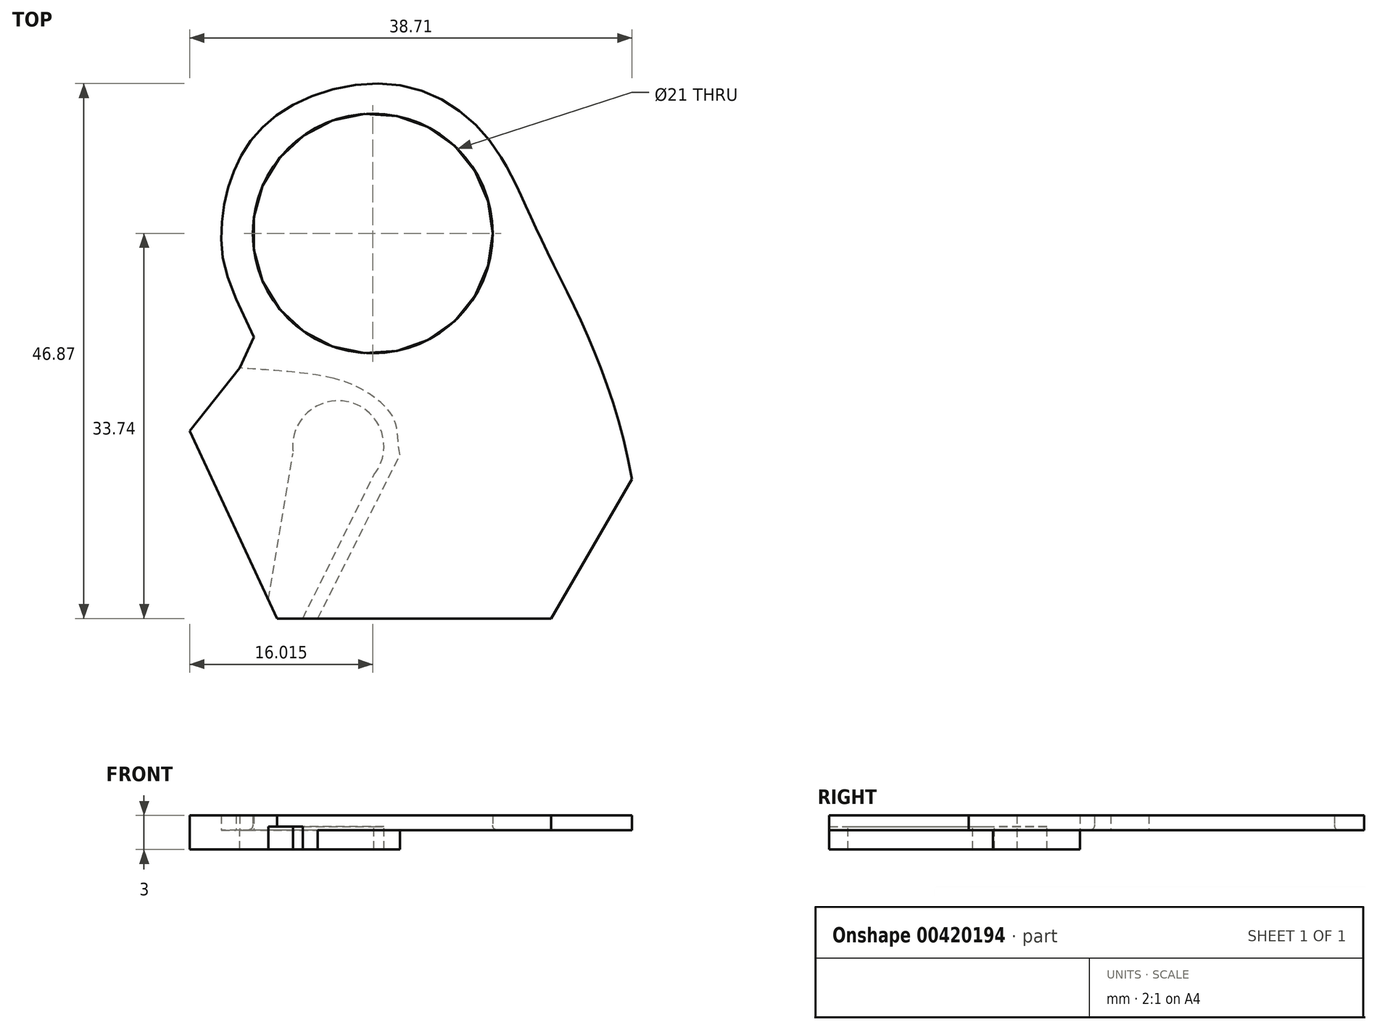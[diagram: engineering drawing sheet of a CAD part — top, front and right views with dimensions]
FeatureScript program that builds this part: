
annotation { "Feature Type Name" : "Feature", "Feature Type Description" : "" }
export const myFeature = defineFeature(function(context is Context, id is Id, definition is map)
    precondition{}
    {
        {
            var Q0;
            Q0=qCreatedBy(makeId("Top.planeOp"),FACE);
            var sketch = newSketch(context, id + "F0", { "sketchPlane" : qUnion([Q0])});
            skLineSegment(sketch, "E0", {"start": v(-18.43, -12.2) * mm, "end": v(5.57, -12.2) * mm});
            skLineSegment(sketch, "E1", {"start": v(5.57, -12.2) * mm, "end": v(12.63, 0) * mm});
            skLineSegment(sketch, "E2", {"start": v(-18.43, -12.2) * mm, "end": v(-26.08, 4.22) * mm});
            skLineSegment(sketch, "E3", {"start": v(-26.08, 4.22) * mm, "end": v(-21.72, 9.75) * mm});
            skLineSegment(sketch, "E4", {"start": v(-21.72, 9.75) * mm, "end": v(-20.49, 12.46) * mm});
            skLineSegment(sketch, "E5", {"start": v(-20.49, 12.46) * mm, "end": v(-22.02, 15.79) * mm});
            skPoint(sketch, "E6", {"position": v(-14.21, 11.55) * mm});
            skPoint(sketch, "E7", {"position": v(0, 25.65) * mm});
            skPoint(sketch, "E8", {"position": v(-2.76, 13.99) * mm});
            skCircle(sketch, "E9", {"center": v(-13.08, 2.87) * mm, "radius": 4 * mm});
            skLineSegment(sketch, "E10", {"start": v(-19.2, -10.55) * mm, "end": v(-17.04, 2.25) * mm});
            skCircle(sketch, "E11", {"center": v(-10.06, 21.53) * mm, "radius": 10.5 * mm});
            skFitSpline(sketch, "E12", {"points": [v(12.63, 0) * mm, v(4.58, 21.25) * mm, v(0, 29.89) * mm, v(-7.31, 34.44) * mm, v(-16.64, 33) * mm, v(-21.43, 28.61) * mm, v(-23.23, 23.05) * mm, v(-22.02, 15.79) * mm], "startDerivative": vector(-21.08, 123.93) * mm, "endDerivative": vector(32.5, -68.62) * mm});
            skLineSegment(sketch, "E13", {"start": v(-16.19, -12.2) * mm, "end": v(-9.96, 0.37) * mm});
            skLineSegment(sketch, "E14", {"start": v(-14.87, -12.2) * mm, "end": v(-7.68, 2.12) * mm});
            skFitSpline(sketch, "E15", {"points": [v(-7.68, 2.12) * mm, v(-8.09, 4.98) * mm, v(-9.8, 7.08) * mm, v(-13.47, 8.82) * mm, v(-21.72, 9.75) * mm], "startDerivative": vector(-2.98, 13.48) * mm, "endDerivative": vector(-25.45, 2.14) * mm});
            skFitSpline(sketch, "E16", {"points": [v(-13.47, 8.82) * mm, v(-5.9, 10.04) * mm, v(0, 14.72) * mm, v(2.32, 21.18) * mm, v(1.19, 28.2) * mm], "startDerivative": vector(31.3, 2.08) * mm, "endDerivative": vector(-12.19, 34.82) * mm});
            skSolve(sketch);
        }
        {
            var Q0;
            {var subQ1=sQuery(id+"F0.wireOp",EDGE,"E1");Q0=makeQuery(id+"F0.imprint","IMPRINT",FACE,{"disambiguationData":[TD([[makeQuery(id+"F0.imprint","IMPRINT",EDGE,{"derivedFrom":subQ1}),1.0]])]});}
            var Q1;
            {var subQ0=sQuery(id+"F0.wireOp",EDGE,"IfHuGSsR-vCJs-cmrE-FMUr-xnXJOKSj7Pgt");Q1=makeQuery(id+"F0.imprint","IMPRINT",FACE,{"disambiguationData":[TD([[makeQuery(id+"F0.imprint","IMPRINT",EDGE,{"derivedFrom":subQ0}),1.0]])]});}
            var Q2;
            {var subQ6=sQuery(id+"F0.wireOp",EDGE,"E3");Q2=makeQuery(id+"F0.imprint","IMPRINT",FACE,{"disambiguationData":[TD([[makeQuery(id+"F0.imprint","IMPRINT",EDGE,{"derivedFrom":subQ6}),-1.0]])]});}
            var Q3;
            {var subQ4=sQuery(id+"F0.wireOp",EDGE,"E4");Q3=makeQuery(id+"F0.imprint","IMPRINT",FACE,{"disambiguationData":[TD([[makeQuery(id+"F0.imprint","IMPRINT",EDGE,{"derivedFrom":subQ4}),-1.0]])]});}
            var Q4;
            {var subQ1=sQuery(id+"F0.wireOp",EDGE,"IfHuGSsR-vCJs-cmrE-FMUr-xnXJOKSj7Pgt");Q4=makeQuery(id+"F0.imprint","IMPRINT",FACE,{"disambiguationData":[TD([[makeQuery(id+"F0.imprint","IMPRINT",EDGE,{"derivedFrom":subQ1}),-1.0]])]});}
            var Q5;
            {var subQ7=sQuery(id+"F0.wireOp",EDGE,"yU8fzeZD-zv5a-J1s4-8gyM-vlChJAQi1y5g");Q5=makeQuery(id+"F0.imprint","IMPRINT",FACE,{"disambiguationData":[TD([[makeQuery(id+"F0.imprint","IMPRINT",EDGE,{"derivedFrom":subQ7}),1.0]])]});}
            var Q6;
            {var subQ0=sQuery(id+"F0.wireOp",EDGE,"E9");var subQ1=makeQuery(id+"F0.imprint","INTERSECT",VERTEX,{"derivedFrom":[subQ0,sQuery(id+"F0.wireOp",EDGE,"E10")]});Q6=makeQuery(id+"F0.imprint","IMPRINT",FACE,{"disambiguationData":[TD([[makeQuery(id+"F0.imprint","IMPRINT",EDGE,{"disambiguationData":[TD([[subQ1,-1.0]])],"derivedFrom":subQ0}),1.0]])]});}
            var Q7;
            {var subQ0=sQuery(id+"F0.wireOp",EDGE,"E10");Q7=makeQuery(id+"F0.imprint","IMPRINT",FACE,{"disambiguationData":[TD([[makeQuery(id+"F0.imprint","IMPRINT",EDGE,{"derivedFrom":subQ0}),-1.0]])]});}
            extrude(context, id + "F1", {"entities" : qUnion([Q0, Q1, Q2, Q3, Q4, Q5, Q6, Q7]), "depth" : 1 * mm, "offsetDistance" : 25 * mm});
        }
        {
            var Q0;
            {var subQ3=sQuery(id+"F0.wireOp",EDGE,"E3");Q0=makeQuery(id+"F0.imprint","IMPRINT",FACE,{"disambiguationData":[TD([[makeQuery(id+"F0.imprint","IMPRINT",EDGE,{"derivedFrom":subQ3}),-1.0]])]});}
            extrude(context, id + "F2", {"entities" : qUnion([Q0]), "operationType" : NewBodyOperationType.ADD, "depth" : 0 * mm, "hasSecondDirection" : true, "secondDirectionOppositeDirection" : true, "secondDirectionDepth" : 2 * mm, "offsetDistance" : 25 * mm});
        }
        {
            var Q0;
            {var subQ3=sQuery(id+"F0.wireOp",EDGE,"E4");Q0=makeQuery(id+"F0.imprint","IMPRINT",FACE,{"disambiguationData":[TD([[makeQuery(id+"F0.imprint","IMPRINT",EDGE,{"derivedFrom":subQ3}),-1.0]])]});}
            var Q1;
            {var subQ2=sQuery(id+"F0.wireOp",EDGE,"E1");Q1=makeQuery(id+"F0.imprint","IMPRINT",FACE,{"disambiguationData":[TD([[makeQuery(id+"F0.imprint","IMPRINT",EDGE,{"derivedFrom":subQ2}),1.0]])]});}
            extrude(context, id + "F3", {"entities" : qUnion([Q0, Q1]), "operationType" : NewBodyOperationType.ADD, "oppositeDirection" : true, "depth" : .3 * mm, "offsetDistance" : 25 * mm});
        }
        {
            var Q0;
            Q0=makeQuery(id+"F3.opExtrude","CAP_EDGE",EDGE,{"disambiguationData":[OSD([sQuery(id+"F0.wireOp",EDGE,"E11")])],"isStart":false});
            fillet(context, id + "F4", {"entities" : qUnion([Q0]), "radius" : .5 * mm, "tangentPropagation" : true, "rho" : 0.5, "crossSection" : FilletCrossSection.CONIC, "allowEdgeOverflow" : false});
        }
    });
